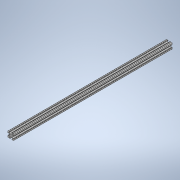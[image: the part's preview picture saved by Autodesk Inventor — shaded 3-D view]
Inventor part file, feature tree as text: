
AUTODESK INVENTOR PART (.ipt)
format: ipt  version: 2020 (Build 240168000, 168)  size: 237,568 bytes
history: native  units: in
note: dims shown in document units (in); Inventor stores cm internally (conversion verified against a paired STEP export)
features: extrude x1, sketch x1
ambient origin geometry x8: Origin, YZ Plane, XZ Plane, XY Plane, X Axis, Y Axis, Z Axis, Center Point
bodies: Solid1 (feature_tree)
feature tree (2):
  extrude  "Extrusion1"  [1 undecoded]
  sketch  "Sketch1"  dims[d0=26.0in d1=0.0in]
note: 1 required parameter value undecoded (feature->parameter linkage not recoverable at this tier; creation-order binding heuristic only, values carry confidence <= 0.55)
